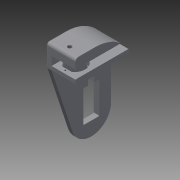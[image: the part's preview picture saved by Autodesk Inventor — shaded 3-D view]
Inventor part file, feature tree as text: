
AUTODESK INVENTOR PART (.ipt)
format: ipt  version: 2015 (Build 190159000, 159)  size: 529,408 bytes
history: native  units: mm
features: sketch x37, extrude x33, fillet x4
ambient origin geometry x8: Origin, YZ Plane, XZ Plane, XY Plane, X Axis, Y Axis, Z Axis, Center Point
bodies: Solid1 (feature_tree)
feature tree (74):
  extrude  "Extrusion1"  Depth=66.3mm
  extrude  "Extrusion2"  Depth=55.0mm
  extrude  "Extrusion3"  Depth=55.0mm
  extrude  "Extrusion4"  Depth=9.9mm
  extrude  "Extrusion5"  Depth=9.9mm
  extrude  "Extrusion6"  Depth=3.0mm
  extrude  "Extrusion7"  Depth=3.0mm
  extrude  "Extrusion8"  Depth=13.6mm
  extrude  "Extrusion9"  Depth=45.0mm
  sketch  "Sketch10"  dims[d22=15.0mm d23=5.0mm d24=0.0mm]
  extrude  "Extrusion10"  Depth=5.0mm TaperAngle=0.0deg
  extrude  "Extrusion11"  Depth=55.0mm
  extrude  "Extrusion12"  Depth=20.0mm
  sketch  "Sketch14"  dims[d33=10.0mm d34=32.9mm d35=0.0mm]
  extrude  "Extrusion13"  Depth=5.0mm TaperAngle=0.0deg
  extrude  "Extrusion14"  Depth=10.0mm TaperAngle=0.0deg
  extrude  "Extrusion15"  Depth=25.0mm
  extrude  "Extrusion16"  Depth=10.0mm TaperAngle=0.0deg
  extrude  "Extrusion17"  Depth=15.0mm
  sketch  "Sketch20"  dims[d50=28.0mm d51=5.0mm d52=0.0mm]
  extrude  "Extrusion18"  Depth=10.0mm
  extrude  "Extrusion19"  Depth=32.9mm TaperAngle=0.0deg
  extrude  "Extrusion20"  Depth=5.0mm TaperAngle=0.0deg
  extrude  "Extrusion21"  Depth=10.0mm
  extrude  "Extrusion22"  Depth=13.6mm
  extrude  "Extrusion23"  Depth=10.0mm
  sketch  "Sketch27"  dims[d68=21.4mm d69=2.0mm]
  extrude  "Extrusion24"  Depth=12.2mm
  extrude  "Extrusion25"  Depth=5.0mm TaperAngle=0.0deg
  extrude  "Extrusion26"  Depth=2.0mm
  extrude  "Extrusion27"  Depth=2.0mm
  sketch  "Sketch32"  dims[d81=2.0mm d82=5.0mm d83=0.0mm]
  sketch  "Sketch33"  dims[d84=45.0mm d86=5.0mm d87=5.0mm d88=39.0mm d89=0.0mm d90=22.0mm]
  extrude  "Extrusion28"  Depth=2.05mm
  extrude  "Extrusion29"  Depth=5.0mm TaperAngle=0.0deg
  extrude  "Extrusion30"  Depth=2.05mm
  extrude  "Extrusion31"  Depth=2.0mm
  fillet  "Fillet1"  Radius=2.05mm
  extrude  "Extrusion32"  Depth=2.0mm TaperAngle=0.0deg
  extrude  "Extrusion33"  Depth=5.0mm
  fillet  "Fillet2"  Radius=5.0mm
  fillet  "Fillet3"  Radius=39.0mm
  fillet  "Fillet4"  Radius=22.0mm
  sketch  "Sketch1"  dims[d0=33.15mm d2=66.3mm]
  sketch  "Sketch2"  dims[d4=18.1mm d5=55.0mm]
  sketch  "Sketch3"  dims[d6=20.0mm d7=55.0mm]
  sketch  "Sketch4"  dims[d8=40.2mm d9=9.9mm]
  sketch  "Sketch5"  dims[d10=9.5mm d11=9.9mm]
  sketch  "Sketch6"  dims[d12=9.5mm d13=3.0mm]
  sketch  "Sketch7"  dims[d14=3.0mm d15=3.0mm]
  sketch  "Sketch8"  dims[d16=3.0mm d17=13.6mm]
  sketch  "Sketch9"  dims[d20=25.0mm d21=45.0mm]
  sketch  "Sketch11"  dims[d25=18.1mm d26=55.0mm]
  sketch  "Sketch12"  dims[d27=40.2mm d28=20.0mm]
  sketch  "Sketch13"  dims[d29=5.0mm d30=0.0mm d31=5.0mm d32=0.0mm]
  sketch  "Sketch15"  dims[d36=25.0mm d37=0.0mm d38=25.0mm]
  sketch  "Sketch16"  dims[d39=10.0mm d40=5.0mm d41=0.0mm]
  sketch  "Sketch17"  dims[d42=12.5mm d43=15.0mm]
  sketch  "Sketch18"  dims[d44=10.0mm d45=0.0mm d46=18.0mm]
  sketch  "Sketch19"  dims[d47=5.0mm d48=32.9mm d49=0.0mm]
  sketch  "Sketch21"  dims[d53=10.0mm d54=0.0mm d55=5.0mm]
  sketch  "Sketch22"  dims[d56=12.5mm d57=13.6mm]
  sketch  "Sketch23"  dims[d58=10.0mm d59=0.0mm d60=12.5mm]
  sketch  "Sketch24"  dims[d61=12.4mm d62=12.2mm]
  sketch  "Sketch25"  dims[d63=6.2mm d64=5.0mm d65=0.0mm]
  sketch  "Sketch26"  dims[d66=10.6mm d67=2.0mm]
  sketch  "Sketch28"  dims[d70=5.0mm d71=0.0mm d72=2.05mm]
  sketch  "Sketch29"  dims[d73=2.05mm d74=5.0mm d75=0.0mm]
  sketch  "Sketch30"  dims[d76=21.4mm d77=2.05mm]
  sketch  "Sketch31"  dims[d78=2.0mm d79=10.6mm d80=2.05mm]
  sketch  "Sketch34"  dims[d91=5.0mm d92=0.0mm]
  sketch  "Sketch35"  dims[d93=3.0mm d94=0.0mm]
  sketch  "Sketch36"  dims[d95=10.0mm]
  sketch  "Sketch37"  dims[d96=2.0mm d97=0.0mm d98=2.0mm d99=0.0mm d100=10.25mm d101=7.25mm d102=22.0mm d103=0.0mm d104=10.0mm d105=2.0mm d106=0.0mm d107=10.0mm d108=3.0mm d109=0.0mm d111=14.0mm d112=14.0mm d113=5.0mm d114=0.0mm d115=29.9mm d116=0.0mm d117=70.0mm d118=0.0mm d119=68.0mm d120=2.0mm d121=5.0mm d122=37.9mm d123=0.0mm d124=28.0mm d125=70.0mm d126=25.0mm d127=25.0mm d128=50.0mm d129=37.9mm d130=0.0mm d131=8.0mm d132=0.0mm d133=12.0mm d134=90.0deg d135=29.9mm d136=0.0mm d137=47.0mm d138=8.0mm d139=8.0mm d140=0.0mm d141=1.0mm d142=5.45mm d143=8.0mm d144=10.0mm d145=0.0mm d146=5.0mm d147=2.0mm d148=0.0mm d149=4.0mm d150=2.0mm d151=2.0mm]
